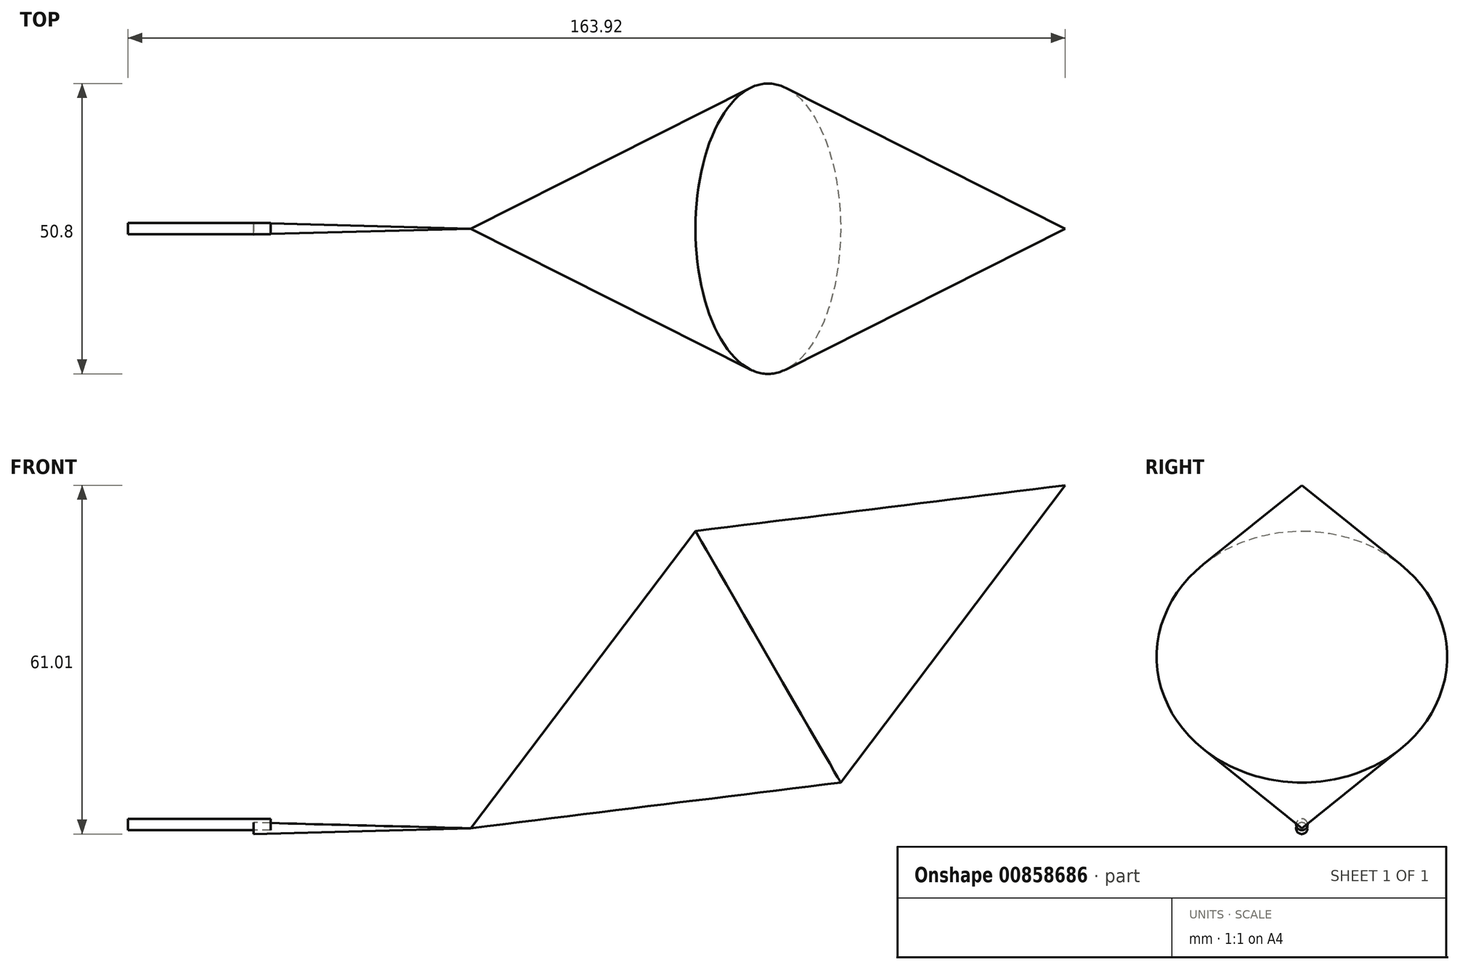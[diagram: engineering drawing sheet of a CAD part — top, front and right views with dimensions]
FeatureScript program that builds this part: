
annotation { "Feature Type Name" : "Feature", "Feature Type Description" : "" }
export const myFeature = defineFeature(function(context is Context, id is Id, definition is map)
    precondition{}
    {
        {
            var Q0;
            Q0=qCreatedBy(makeId("Right.planeOp"),FACE);
            var sketch = newSketch(context, id + "F0", { "sketchPlane" : qUnion([Q0])});
            skCircle(sketch, "E0", {"center": v(0, 0.22) * mm, "radius": 1 * mm});
            skSolve(sketch);
        }
        {
            var Q0;
            Q0=makeQuery(id+"F0.imprint","IMPRINT",FACE,{"disambiguationData":[TD([[makeQuery(id+"F0.imprint","IMPRINT",EDGE,{"derivedFrom":sQuery(id+"F0.wireOp",EDGE,"E0")}),1.0]])]});
            extrude(context, id + "F1", {"entities" : qUnion([Q0]), "depth" : 25 * mm, "offsetDistance" : 25 * mm});
        }
        {
            var Q0;
            Q0=qCreatedBy(makeId("Front.planeOp"),FACE);
            var sketch = newSketch(context, id + "F2", { "sketchPlane" : qUnion([Q0])});
            skLineSegment(sketch, "E1", {"start": v(26.14, 0) * mm, "end": v(26.14, 1) * mm});
            skLineSegment(sketch, "E2", {"start": v(26.14, 0) * mm, "end": v(64.14, 0) * mm});
            skLineSegment(sketch, "E3", {"start": v(26.14, 1) * mm, "end": v(64.14, 0) * mm});
            skSolve(sketch);
        }
        {
            var Q0;
            Q0=makeQuery(id+"F2.imprint","IMPRINT",FACE,{"disambiguationData":[TD([[makeQuery(id+"F2.imprint","IMPRINT",EDGE,{"derivedFrom":sQuery(id+"F2.wireOp",EDGE,"E1")}),-1.0]])]});
            var Q1;
            Q1=sQuery(id+"F2.wireOp",EDGE,"E2");
            revolve(context, id + "F3", {"surfaceOperationType" : NewSurfaceOperationType.NEW, "entities" : qUnion([Q0]), "axis" : qUnion([Q1]), "revolveType" : RevolveType.FULL});
        }
        {
            var Q0;
            Q0=makeQuery(id+"F3.opRevolve","SWEPT_BODY",BODY,{"disambiguationData":[OSD([sQuery(id+"F2.wireOp",EDGE,"E1"),sQuery(id+"F2.wireOp",EDGE,"E2"),sQuery(id+"F2.wireOp",EDGE,"E3")])]});
            transform(context, id + "F4", {"entities" : qUnion([Q0]), "transformType" : TransformType.TRANSLATION_3D, "dx" : 0 * mm, "dy" : 0 * mm, "dz" : 0.23 * mm, "makeCopy" : false});
        }
        {
            var Q0;
            Q0=makeQuery(id+"F3.opRevolve","SWEPT_BODY",BODY,{"disambiguationData":[OSD([sQuery(id+"F2.wireOp",EDGE,"E1"),sQuery(id+"F2.wireOp",EDGE,"E2"),sQuery(id+"F2.wireOp",EDGE,"E3")])]});
            transform(context, id + "F5", {"entities" : qUnion([Q0]), "transformType" : TransformType.TRANSLATION_3D, "dx" : -1.18 * mm, "dy" : -0.01 * mm, "dz" : 0 * mm, "makeCopy" : false});
        }
        {
            var Q0;
            Q0=qCreatedBy(makeId("Front.planeOp"),FACE);
            var sketch = newSketch(context, id + "F6", { "sketchPlane" : qUnion([Q0])});
            skLineSegment(sketch, "E4", {"start": v(62.96, 0.24) * mm, "end": v(166.88, 60.24) * mm});
            skLineSegment(sketch, "E5", {"start": v(114.92, 30.24) * mm, "end": v(102.22, 52.24) * mm});
            skLineSegment(sketch, "E6", {"start": v(62.96, 0.24) * mm, "end": v(102.22, 52.24) * mm});
            skLineSegment(sketch, "E7", {"start": v(102.22, 52.24) * mm, "end": v(166.88, 60.24) * mm});
            skSolve(sketch);
        }
        {
            var Q0;
            {var subQ2=sQuery(id+"F6.wireOp",EDGE,"E5");Q0=makeQuery(id+"F6.imprint","IMPRINT",FACE,{"disambiguationData":[TD([[makeQuery(id+"F6.imprint","IMPRINT",EDGE,{"derivedFrom":subQ2}),-1.0]])]});}
            var Q1;
            {var subQ2=sQuery(id+"F6.wireOp",EDGE,"E5");Q1=makeQuery(id+"F6.imprint","IMPRINT",FACE,{"disambiguationData":[TD([[makeQuery(id+"F6.imprint","IMPRINT",EDGE,{"derivedFrom":subQ2}),1.0]])]});}
            var Q2;
            Q2=sQuery(id+"F6.wireOp",EDGE,"E4");
            revolve(context, id + "F7", {"surfaceOperationType" : NewSurfaceOperationType.NEW, "entities" : qUnion([Q0, Q1]), "axis" : qUnion([Q2]), "revolveType" : RevolveType.FULL});
        }
        {
            var Q0;
            Q0=makeQuery(id+"F1.opExtrude","SWEPT_BODY",BODY,{"disambiguationData":[OSD([sQuery(id+"F0.wireOp",EDGE,"E0")])]});
            transform(context, id + "F8", {"entities" : qUnion([Q0]), "transformType" : TransformType.TRANSLATION_3D, "dx" : 2.96 * mm, "dy" : 4.34E-16 * mm, "dz" : 0.67 * mm, "makeCopy" : false});
        }
    });
